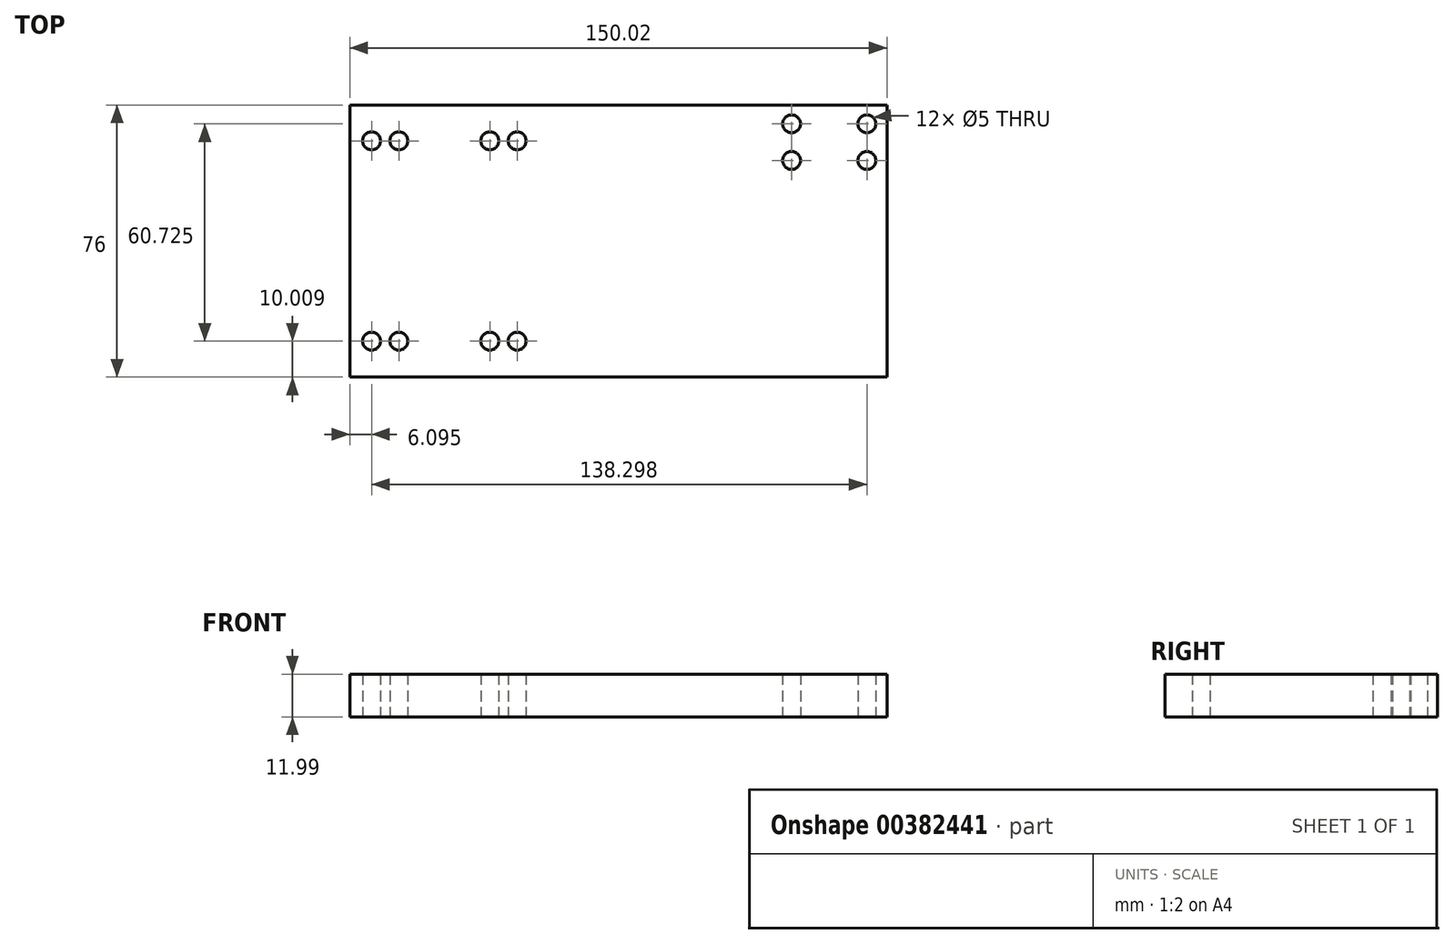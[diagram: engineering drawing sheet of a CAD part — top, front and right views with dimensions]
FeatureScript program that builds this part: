
annotation { "Feature Type Name" : "Feature", "Feature Type Description" : "" }
export const myFeature = defineFeature(function(context is Context, id is Id, definition is map)
    precondition{}
    {
        {
            var Q0;
            Q0=qCreatedBy(makeId("Top.planeOp"),FACE);
            var sketch = newSketch(context, id + "F0", { "sketchPlane" : qUnion([Q0])});
            skLineSegment(sketch, "E0.bottom", {"start": v(-75, 38) * mm, "end": v(75, 38) * mm});
            skLineSegment(sketch, "E0.top", {"start": v(-75, -38) * mm, "end": v(75, -38) * mm});
            skLineSegment(sketch, "E0.left", {"start": v(-75, 38) * mm, "end": v(-75, -38) * mm});
            skLineSegment(sketch, "E0.right", {"start": v(75, 38) * mm, "end": v(75, -38) * mm});
            skPoint(sketch, "E0.middle", {"position": v(0, 0) * mm});
            skCircle(sketch, "E1", {"center": v(69.38, 32.73) * mm, "radius": 2.5 * mm});
            skCircle(sketch, "E2", {"center": v(48.35, 32.73) * mm, "radius": 2.5 * mm});
            skCircle(sketch, "E3", {"center": v(69.38, 22.5) * mm, "radius": 2.5 * mm});
            skCircle(sketch, "E4", {"center": v(48.35, 22.5) * mm, "radius": 2.5 * mm});
            skCircle(sketch, "E5", {"center": v(-68.92, 28) * mm, "radius": 2.5 * mm});
            skCircle(sketch, "E6", {"center": v(-28.28, 28) * mm, "radius": 2.5 * mm});
            skCircle(sketch, "E7", {"center": v(-28.28, -28) * mm, "radius": 2.5 * mm});
            skCircle(sketch, "E8", {"center": v(-68.92, -28) * mm, "radius": 2.5 * mm});
            skPoint(sketch, "E9.middle", {"position": v(-48.6, 0) * mm});
            skCircle(sketch, "E10", {"center": v(-61.3, 28) * mm, "radius": 2.5 * mm});
            skCircle(sketch, "E11", {"center": v(-35.9, 28) * mm, "radius": 2.5 * mm});
            skCircle(sketch, "E12", {"center": v(-35.9, -28) * mm, "radius": 2.5 * mm});
            skCircle(sketch, "E13", {"center": v(-61.3, -28) * mm, "radius": 2.5 * mm});
            skSolve(sketch);
        }
        {
            var Q0;
            Q0=makeQuery(id+"F0.imprint","IMPRINT",FACE,{"disambiguationData":[TD([[makeQuery(id+"F0.imprint","IMPRINT",EDGE,{"derivedFrom":sQuery(id+"F0.wireOp",EDGE,"E0.bottom")}),-1.0]])]});
            extrude(context, id + "F1", {"entities" : qUnion([Q0]), "depth" : 12 * mm});
        }
    });
